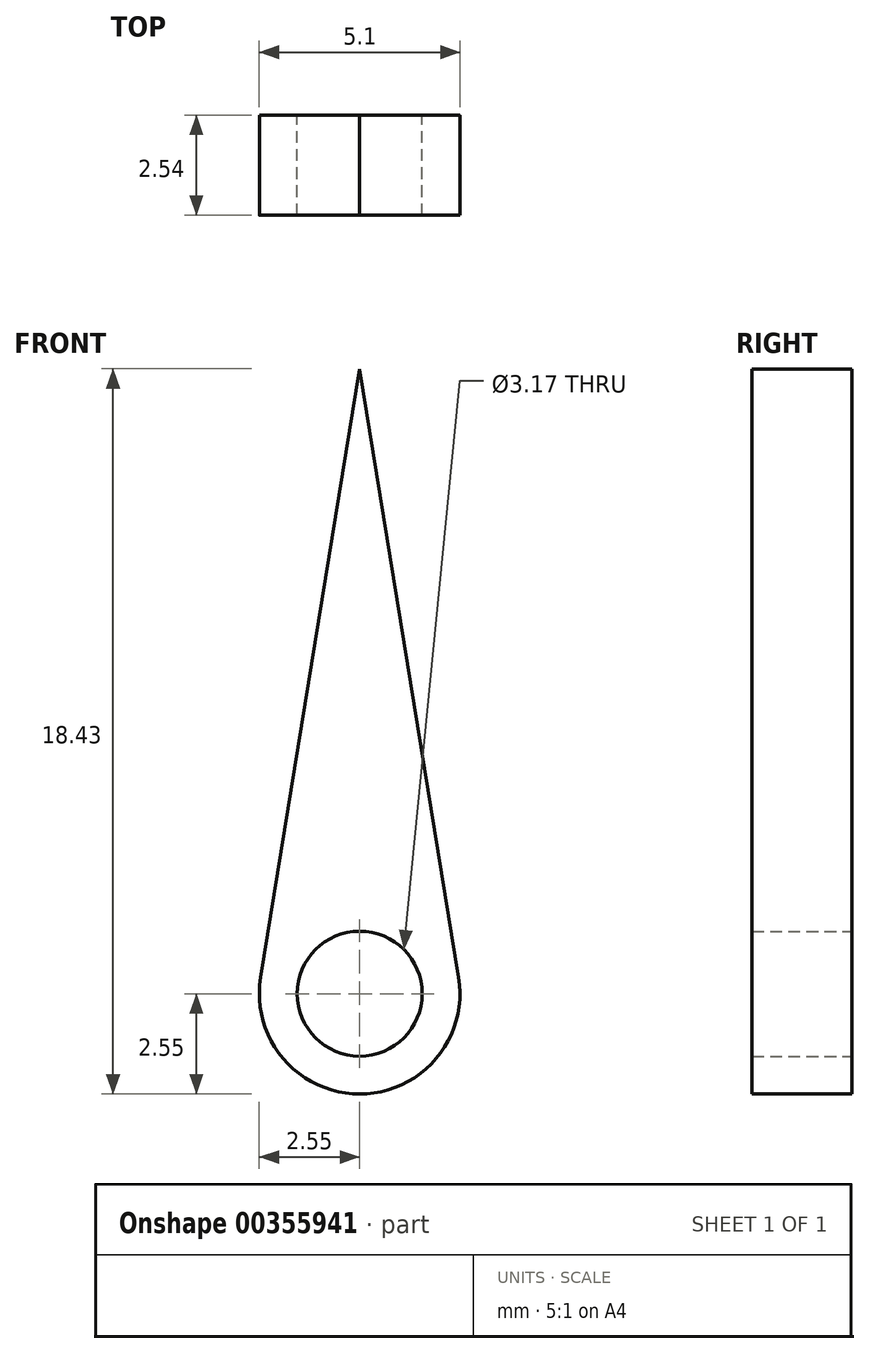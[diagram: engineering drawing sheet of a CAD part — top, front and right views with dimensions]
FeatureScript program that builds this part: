
annotation { "Feature Type Name" : "Feature", "Feature Type Description" : "" }
export const myFeature = defineFeature(function(context is Context, id is Id, definition is map)
    precondition{}
    {
        {
            var Q0;
            Q0=qCreatedBy(makeId("Front.planeOp"),FACE);
            var sketch = newSketch(context, id + "F0", { "sketchPlane" : qUnion([Q0])});
            skCircle(sketch, "E0", {"center": v(0, 0) * mm, "radius": 1.59 * mm});
            skCircle(sketch, "E1", {"center": v(0, 0) * mm, "radius": 2.55 * mm});
            skLineSegment(sketch, "E2", {"start": v(0, 15.88) * mm, "end": v(-2.58, 0) * mm});
            skLineSegment(sketch, "E3", {"start": v(0, 15.88) * mm, "end": v(2.58, 0) * mm});
            skSolve(sketch);
        }
        {
            var Q0;
            Q0=makeQuery(id+"F0.imprint","IMPRINT",FACE,{"disambiguationData":[TD([[makeQuery(id+"F0.imprint","IMPRINT",EDGE,{"derivedFrom":sQuery(id+"F0.wireOp",EDGE,"E0")}),-1.0]])]});
            extrude(context, id + "F1", {"entities" : qUnion([Q0]), "endBound" : BoundingType.SYMMETRIC, "depth" : 2.54 * mm});
        }
        {
            var Q0;
            {var subQ0=sQuery(id+"F0.wireOp",EDGE,"E2");var subQ1=sQuery(id+"F0.wireOp",EDGE,"E1");var subQ2=makeQuery(id+"F0.imprint","INTERSECT",VERTEX,{"derivedFrom":[subQ1,subQ0]});Q0=makeQuery(id+"F0.imprint","IMPRINT",FACE,{"disambiguationData":[TD([[makeQuery(id+"F0.imprint","IMPRINT",EDGE,{"disambiguationData":[TD([[subQ2,1.0]])],"derivedFrom":subQ1}),-1.0]])]});}
            extrude(context, id + "F2", {"entities" : qUnion([Q0]), "operationType" : NewBodyOperationType.ADD, "endBound" : BoundingType.SYMMETRIC, "depth" : 2.54 * mm});
        }
    });
